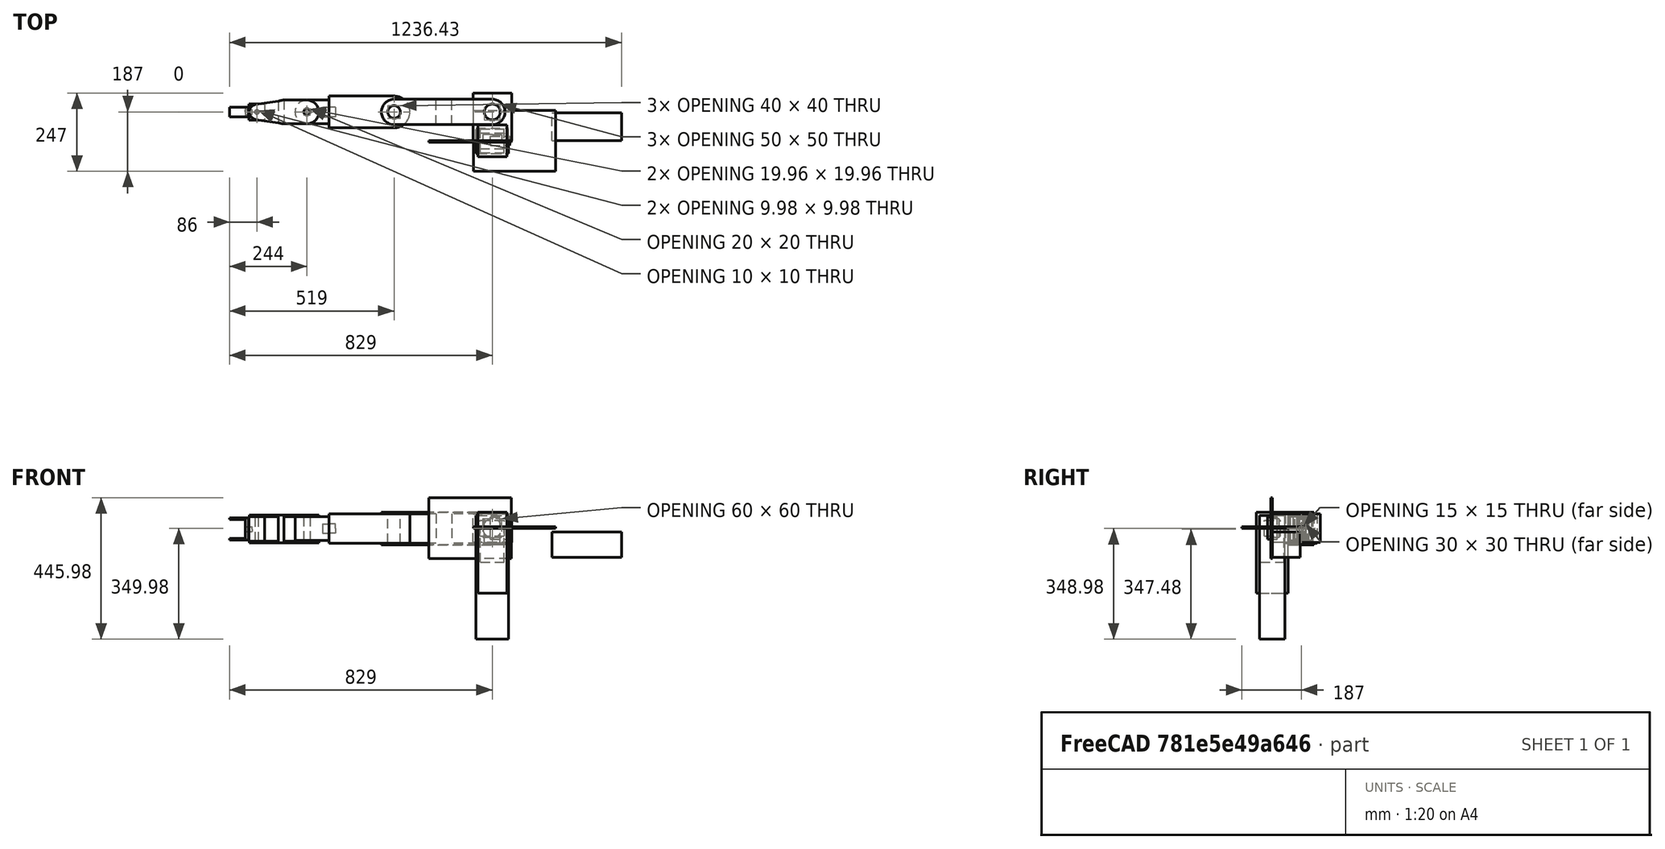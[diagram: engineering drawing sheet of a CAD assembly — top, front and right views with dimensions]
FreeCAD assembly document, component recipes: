
FREECAD ASSEMBLY — COMPONENT RECIPES ("Arm_CAD")

This assembly document has 17 components, labeled P0..P16 below (a component is one placed body or linked part). 0 of them carry a construction recipe — the FreeCAD feature program that regenerates the part from scratch, quoted from this document or its linked companion documents; the rest are supplied as boundary geometry only. No exploded tour is included for this assembly.
COMPONENT P0 — geometry summary ("Arm_asm"; no construction recipe available for this part):
  bounding box: 1236.4 x 446.0 x 247.0 mm
  tessellated surface: 22,208 triangles
  volume: 10796350 mm^3 (8% of its bounding box)
COMPONENT P1 — geometry summary ("collision_l_Base001_"; no construction recipe available for this part):
  bounding box: 260.0 x 192.0 x 5.0 mm
  tessellated surface: 12 triangles
  volume: 249600 mm^3 (100% of its bounding box)
  symmetry: 2-fold rotationally symmetric about the x axis; 2-fold rotationally symmetric about the y axis; 2-fold rotationally symmetric about the z axis; mirror-symmetric across its x mid-plane, y mid-plane, z mid-plane
COMPONENT P2 — geometry summary ("collision_l_Claw001_"; no construction recipe available for this part):
  bounding box: 70.0 x 61.0 x 30.0 mm
  tessellated surface: 12 triangles
  volume: 128100 mm^3 (100% of its bounding box)
  symmetry: 2-fold rotationally symmetric about the x axis; 2-fold rotationally symmetric about the y axis; 2-fold rotationally symmetric about the z axis; mirror-symmetric across its x mid-plane, y mid-plane, z mid-plane
COMPONENT P3 — geometry summary ("collision_l_Link006_"; no construction recipe available for this part):
  bounding box: 151.0 x 122.0 x 90.0 mm
  tessellated surface: 12 triangles
  volume: 1657980 mm^3 (100% of its bounding box)
  symmetry: 2-fold rotationally symmetric about the x axis; 2-fold rotationally symmetric about the y axis; 2-fold rotationally symmetric about the z axis; mirror-symmetric across its x mid-plane, y mid-plane, z mid-plane
COMPONENT P4 — geometry summary ("collision_l_Link007_"; no construction recipe available for this part):
  bounding box: 390.0 x 102.5 x 80.0 mm
  tessellated surface: 12 triangles
  volume: 3197875 mm^3 (100% of its bounding box)
  symmetry: 2-fold rotationally symmetric about the x axis; 2-fold rotationally symmetric about the y axis; 2-fold rotationally symmetric about the z axis; mirror-symmetric across its x mid-plane, y mid-plane, z mid-plane
COMPONENT P5 — geometry summary ("collision_l_Link008_"; no construction recipe available for this part):
  bounding box: 255.0 x 100.0 x 92.0 mm
  tessellated surface: 12 triangles
  volume: 2346000 mm^3 (100% of its bounding box)
  symmetry: 2-fold rotationally symmetric about the x axis; 2-fold rotationally symmetric about the y axis; 2-fold rotationally symmetric about the z axis; mirror-symmetric across its x mid-plane, y mid-plane, z mid-plane
COMPONENT P6 — geometry summary ("collision_l_Link009_"; no construction recipe available for this part):
  bounding box: 107.5 x 75.0 x 75.0 mm
  tessellated surface: 12 triangles
  volume: 604607 mm^3 (100% of its bounding box)
  symmetry: 2-fold rotationally symmetric about the x axis; 2-fold rotationally symmetric about the y axis; 4-fold rotationally symmetric about the z axis; mirror-symmetric across its x mid-plane, y mid-plane, z mid-plane
COMPONENT P7 — geometry summary ("collision_l_Link010_"; no construction recipe available for this part):
  bounding box: 219.2 x 88.0 x 79.4 mm
  tessellated surface: 12 triangles
  volume: 1531762 mm^3 (100% of its bounding box)
  symmetry: 2-fold rotationally symmetric about the x axis; 2-fold rotationally symmetric about the y axis; 2-fold rotationally symmetric about the z axis; mirror-symmetric across its x mid-plane, y mid-plane, z mid-plane
COMPONENT P8 — geometry summary ("collision_l_Link011_"; no construction recipe available for this part):
  bounding box: 78.0 x 50.0 x 50.0 mm
  tessellated surface: 12 triangles
  volume: 195000 mm^3 (100% of its bounding box)
  symmetry: 2-fold rotationally symmetric about the x axis; 4-fold rotationally symmetric about the y axis; 2-fold rotationally symmetric about the z axis; mirror-symmetric across its x mid-plane, y mid-plane, z mid-plane
COMPONENT P9 — geometry summary ("real_l_Base001_"; no construction recipe available for this part):
  bounding box: 260.0 x 192.0 x 5.0 mm
  tessellated surface: 520 triangles
  volume: 235463 mm^3 (94% of its bounding box)
  symmetry: 2-fold rotationally symmetric about the x axis; mirror-symmetric across its y mid-plane, z mid-plane
COMPONENT P10 — geometry summary ("real_l_Claw001_"; no construction recipe available for this part):
  bounding box: 70.0 x 61.0 x 30.0 mm
  tessellated surface: 884 triangles
  volume: 34763 mm^3 (27% of its bounding box)
  symmetry: 2-fold rotationally symmetric about the x axis; mirror-symmetric across its y mid-plane, z mid-plane
COMPONENT P11 — geometry summary ("real_l_Link006_"; no construction recipe available for this part):
  bounding box: 151.0 x 122.0 x 90.0 mm
  tessellated surface: 1,024 triangles
  volume: 1424717 mm^3 (86% of its bounding box)
  symmetry: 2-fold rotationally symmetric about the z axis; mirror-symmetric across its x mid-plane, y mid-plane
COMPONENT P12 — geometry summary ("real_l_Link007_"; no construction recipe available for this part):
  bounding box: 390.0 x 102.5 x 80.0 mm
  tessellated surface: 3,076 triangles
  volume: 638223 mm^3 (20% of its bounding box)
  symmetry: 2-fold rotationally symmetric about the z axis; mirror-symmetric across its x mid-plane, y mid-plane
COMPONENT P13 — geometry summary ("real_l_Link008_"; no construction recipe available for this part):
  bounding box: 255.0 x 100.0 x 92.0 mm
  tessellated surface: 1,276 triangles
  volume: 2117535 mm^3 (90% of its bounding box)
  symmetry: 2-fold rotationally symmetric about the z axis; mirror-symmetric across its x mid-plane, y mid-plane
COMPONENT P14 — geometry summary ("real_l_Link009_"; no construction recipe available for this part):
  bounding box: 107.5 x 75.0 x 75.0 mm
  tessellated surface: 1,232 triangles
  volume: 521721 mm^3 (86% of its bounding box)
  symmetry: 2-fold rotationally symmetric about the z axis; mirror-symmetric across its x mid-plane, y mid-plane
COMPONENT P15 — geometry summary ("real_l_Link010_"; no construction recipe available for this part):
  bounding box: 219.2 x 88.0 x 79.4 mm
  tessellated surface: 2,500 triangles
  volume: 238647 mm^3 (16% of its bounding box)
  symmetry: mirror-symmetric across its y mid-plane
COMPONENT P16 — geometry summary ("real_l_Link011_"; no construction recipe available for this part):
  bounding box: 78.0 x 50.0 x 50.0 mm
  tessellated surface: 592 triangles
  volume: 187107 mm^3 (96% of its bounding box)
  symmetry: 2-fold rotationally symmetric about the x axis; mirror-symmetric across its y mid-plane, z mid-plane
PROVENANCE & LICENSES
A FreeCAD (.FCStd) document from a public repository crawl; recipes are the document's own serialized feature recipes (and, for linked parts, companion documents' recipes).
License: as declared in the source repository (recorded in the dataset sidecar).
